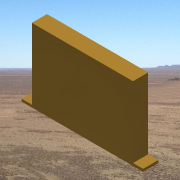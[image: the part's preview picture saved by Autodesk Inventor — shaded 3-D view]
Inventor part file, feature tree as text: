
AUTODESK INVENTOR PART (.ipt)
format: ipt  version: 2014 SP1 (Build 180222100, 222)  size: 115,712 bytes
history: native  units: in
note: dims shown in document units (in); Inventor stores cm internally (conversion verified against a paired STEP export)
features: extrude x1, sketch x1
ambient origin geometry x8: Origin, YZ Plane, XZ Plane, XY Plane, X Axis, Y Axis, Z Axis, Center Point
bodies: Solid1 (feature_tree)
feature tree (2):
  extrude  "Extrusion1"  Depth=0.25in
  sketch  "Sketch1"  dims[d0=12.0in d1=0.25in d2=1.0in d3=7.0in d4=1.5in d5=0.0in]
